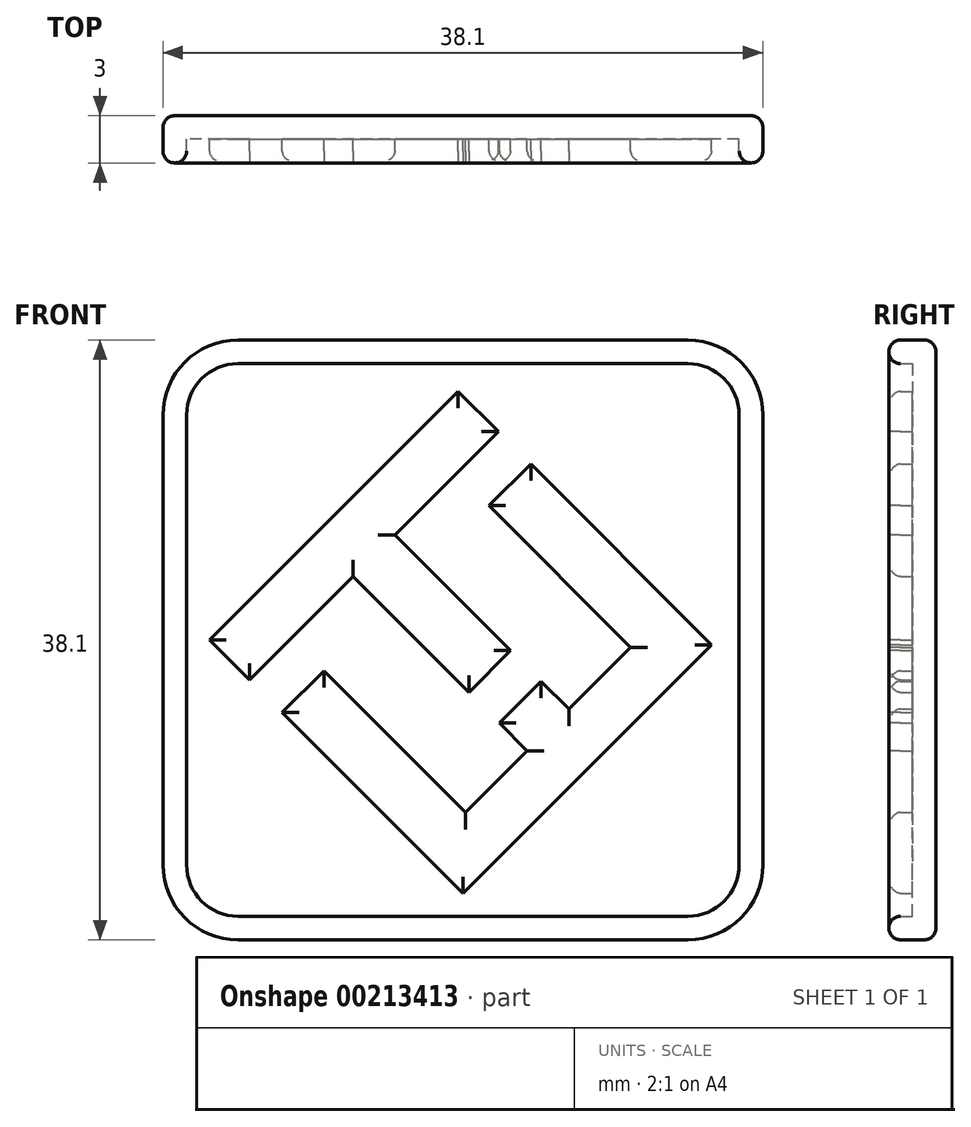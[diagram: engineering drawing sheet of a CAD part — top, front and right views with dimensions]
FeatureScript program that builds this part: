
annotation { "Feature Type Name" : "Feature", "Feature Type Description" : "" }
export const myFeature = defineFeature(function(context is Context, id is Id, definition is map)
    precondition{}
    {
        {
            var Q0;
            Q0=qCreatedBy(makeId("Front.planeOp"),FACE);
            var sketch = newSketch(context, id + "F0", { "sketchPlane" : qUnion([Q0])});
            skLineSegment(sketch, "E0", {"start": v(-14.29, -19.05) * mm, "end": v(14.29, -19.05) * mm});
            skArc(sketch, "E1", {"start": v(14.29, -19.05) * mm, "mid": v(17.66, -17.66) * mm, "end": v(19.05, -14.29) * mm});
            skLineSegment(sketch, "E2", {"start": v(19.05, -14.29) * mm, "end": v(19.05, 14.29) * mm});
            skArc(sketch, "E3", {"start": v(19.05, 14.29) * mm, "mid": v(17.66, 17.66) * mm, "end": v(14.29, 19.05) * mm});
            skLineSegment(sketch, "E4", {"start": v(14.29, 19.05) * mm, "end": v(-14.29, 19.05) * mm});
            skArc(sketch, "E5", {"start": v(-14.29, 19.05) * mm, "mid": v(-17.66, 17.66) * mm, "end": v(-19.05, 14.29) * mm});
            skLineSegment(sketch, "E6", {"start": v(-19.05, 14.29) * mm, "end": v(-19.05, -14.29) * mm});
            skArc(sketch, "E7", {"start": v(-19.05, -14.29) * mm, "mid": v(-17.66, -17.66) * mm, "end": v(-14.29, -19.05) * mm});
            skLineSegment(sketch, "E8", {"start": v(-13.55, -2.55) * mm, "end": v(-6.98, 4.02) * mm});
            skLineSegment(sketch, "E9", {"start": v(-6.98, 4.02) * mm, "end": v(0.37, -3.33) * mm});
            skLineSegment(sketch, "E10", {"start": v(0.37, -3.33) * mm, "end": v(3.03, -0.68) * mm});
            skLineSegment(sketch, "E11", {"start": v(3.03, -0.68) * mm, "end": v(-4.32, 6.67) * mm});
            skLineSegment(sketch, "E12", {"start": v(-13.55, -2.55) * mm, "end": v(-16.1, 0) * mm});
            skLineSegment(sketch, "E13", {"start": v(-16.1, 0) * mm, "end": v(-0.3, 15.8) * mm});
            skLineSegment(sketch, "E14", {"start": v(2.25, 13.24) * mm, "end": v(-0.3, 15.8) * mm});
            skLineSegment(sketch, "E15", {"start": v(-4.32, 6.67) * mm, "end": v(2.25, 13.24) * mm});
            skLineSegment(sketch, "E16", {"start": v(0, -16.1) * mm, "end": v(15.8, -0.3) * mm});
            skLineSegment(sketch, "E17", {"start": v(15.8, -0.3) * mm, "end": v(4.31, 11.17) * mm});
            skLineSegment(sketch, "E18", {"start": v(1.66, 8.52) * mm, "end": v(4.31, 11.17) * mm});
            skLineSegment(sketch, "E19", {"start": v(1.66, 8.52) * mm, "end": v(10.65, -0.47) * mm});
            skLineSegment(sketch, "E20", {"start": v(10.65, -0.47) * mm, "end": v(6.74, -4.39) * mm});
            skLineSegment(sketch, "E21", {"start": v(6.74, -4.39) * mm, "end": v(4.97, -2.62) * mm});
            skLineSegment(sketch, "E22", {"start": v(2.32, -5.27) * mm, "end": v(4.97, -2.62) * mm});
            skLineSegment(sketch, "E23", {"start": v(0, -16.1) * mm, "end": v(-11.48, -4.62) * mm});
            skLineSegment(sketch, "E24", {"start": v(-8.83, -1.97) * mm, "end": v(-11.48, -4.62) * mm});
            skLineSegment(sketch, "E25", {"start": v(-8.83, -1.97) * mm, "end": v(0.17, -10.96) * mm});
            skLineSegment(sketch, "E26", {"start": v(0.17, -10.96) * mm, "end": v(4.08, -7.04) * mm});
            skLineSegment(sketch, "E27", {"start": v(4.08, -7.04) * mm, "end": v(2.32, -5.27) * mm});
            skSolve(sketch);
        }
        {
            var Q0;
            Q0 = qSketchRegion(id + "F0", true);
            extrude(context, id + "F1", {"entities" : qUnion([Q0]), "depth" : 1.5 * mm});
        }
        {
            var Q0;
            Q0=makeQuery(id+"F0.imprint","IMPRINT",FACE,{"disambiguationData":[TD([[makeQuery(id+"F0.imprint","IMPRINT",EDGE,{"derivedFrom":sQuery(id+"F0.wireOp",EDGE,"E8")}),1.0]])]});
            var Q1;
            Q1=makeQuery(id+"F0.imprint","IMPRINT",FACE,{"disambiguationData":[TD([[makeQuery(id+"F0.imprint","IMPRINT",EDGE,{"derivedFrom":sQuery(id+"F0.wireOp",EDGE,"E16")}),1.0]])]});
            extrude(context, id + "F2", {"entities" : qUnion([Q0, Q1]), "operationType" : NewBodyOperationType.ADD, "depth" : 3 * mm});
        }
        {
            var Q0;
            Q0=makeQuery(id+"F0.imprint","IMPRINT",FACE,{"disambiguationData":[TD([[makeQuery(id+"F0.imprint","IMPRINT",EDGE,{"derivedFrom":sQuery(id+"F0.wireOp",EDGE,"E0")}),1.0]])]});
            var sketch = newSketch(context, id + "F3", { "sketchPlane" : qUnion([Q0])});
            skLineSegment(sketch, "E28.0.0", {"start": v(-19.05, 14.29) * mm, "end": v(-19.05, -14.29) * mm});
            skArc(sketch, "E28.0.1", {"start": v(-19.05, -14.29) * mm, "mid": v(-17.66, -17.66) * mm, "end": v(-14.29, -19.05) * mm});
            skLineSegment(sketch, "E28.0.2", {"start": v(-14.29, -19.05) * mm, "end": v(14.29, -19.05) * mm});
            skArc(sketch, "E28.0.3", {"start": v(14.29, -19.05) * mm, "mid": v(17.66, -17.66) * mm, "end": v(19.05, -14.29) * mm});
            skLineSegment(sketch, "E28.0.4", {"start": v(19.05, -14.29) * mm, "end": v(19.05, 14.29) * mm});
            skArc(sketch, "E28.0.5", {"start": v(19.05, 14.29) * mm, "mid": v(17.66, 17.66) * mm, "end": v(14.29, 19.05) * mm});
            skLineSegment(sketch, "E28.0.6", {"start": v(14.29, 19.05) * mm, "end": v(-14.29, 19.05) * mm});
            skArc(sketch, "E28.0.7", {"start": v(-14.29, 19.05) * mm, "mid": v(-17.66, 17.66) * mm, "end": v(-19.05, 14.29) * mm});
            skArc(sketch, "E29.0", {"start": v(-14.29, 17.55) * mm, "mid": v(-16.6, 16.6) * mm, "end": v(-17.55, 14.29) * mm});
            skLineSegment(sketch, "E29.1", {"start": v(14.29, 17.55) * mm, "end": v(-14.29, 17.55) * mm});
            skLineSegment(sketch, "E29.2", {"start": v(-17.55, 14.29) * mm, "end": v(-17.55, -14.29) * mm});
            skArc(sketch, "E29.3", {"start": v(17.55, 14.29) * mm, "mid": v(16.6, 16.6) * mm, "end": v(14.29, 17.55) * mm});
            skArc(sketch, "E29.4", {"start": v(-17.55, -14.29) * mm, "mid": v(-16.6, -16.6) * mm, "end": v(-14.29, -17.55) * mm});
            skLineSegment(sketch, "E29.5", {"start": v(-14.29, -17.55) * mm, "end": v(14.29, -17.55) * mm});
            skArc(sketch, "E29.6", {"start": v(14.29, -17.55) * mm, "mid": v(16.6, -16.6) * mm, "end": v(17.55, -14.29) * mm});
            skLineSegment(sketch, "E29.7", {"start": v(17.55, -14.29) * mm, "end": v(17.55, 14.29) * mm});
            skSolve(sketch);
        }
        {
            var Q0;
            Q0=makeQuery(id+"F3.imprint","IMPRINT",FACE,{"disambiguationData":[TD([[makeQuery(id+"F3.imprint","IMPRINT",EDGE,{"derivedFrom":sQuery(id+"F3.wireOp",EDGE,"E28.0.0")}),1.0]])]});
            extrude(context, id + "F4", {"entities" : qUnion([Q0]), "operationType" : NewBodyOperationType.ADD, "depth" : 3 * mm});
        }
        {
            var Q0;
            Q0=makeQuery(id+"F2.opExtrude","CAP_FACE",FACE,{"disambiguationData":[OSD([sQuery(id+"F0.wireOp",EDGE,"E16"),sQuery(id+"F0.wireOp",EDGE,"E17"),sQuery(id+"F0.wireOp",EDGE,"E18"),sQuery(id+"F0.wireOp",EDGE,"E19"),sQuery(id+"F0.wireOp",EDGE,"E20"),sQuery(id+"F0.wireOp",EDGE,"E21"),sQuery(id+"F0.wireOp",EDGE,"E22"),sQuery(id+"F0.wireOp",EDGE,"E23"),sQuery(id+"F0.wireOp",EDGE,"E24"),sQuery(id+"F0.wireOp",EDGE,"E25"),sQuery(id+"F0.wireOp",EDGE,"E26"),sQuery(id+"F0.wireOp",EDGE,"E27")])],"isStart":false});
            var Q1;
            Q1=makeQuery(id+"F2.opExtrude","CAP_FACE",FACE,{"disambiguationData":[OSD([sQuery(id+"F0.wireOp",EDGE,"E8"),sQuery(id+"F0.wireOp",EDGE,"E9"),sQuery(id+"F0.wireOp",EDGE,"E10"),sQuery(id+"F0.wireOp",EDGE,"E11"),sQuery(id+"F0.wireOp",EDGE,"E12"),sQuery(id+"F0.wireOp",EDGE,"E13"),sQuery(id+"F0.wireOp",EDGE,"E14"),sQuery(id+"F0.wireOp",EDGE,"E15")])],"isStart":false});
            var Q2;
            Q2=makeQuery(id+"F4.opExtrude","CAP_FACE",FACE,{"disambiguationData":[OSD([sQuery(id+"F3.wireOp",EDGE,"E28.0.0"),sQuery(id+"F3.wireOp",EDGE,"E28.0.1"),sQuery(id+"F3.wireOp",EDGE,"E28.0.2"),sQuery(id+"F3.wireOp",EDGE,"E28.0.3"),sQuery(id+"F3.wireOp",EDGE,"E28.0.4"),sQuery(id+"F3.wireOp",EDGE,"E28.0.5"),sQuery(id+"F3.wireOp",EDGE,"E28.0.6"),sQuery(id+"F3.wireOp",EDGE,"E28.0.7"),sQuery(id+"F3.wireOp",EDGE,"E29.0"),sQuery(id+"F3.wireOp",EDGE,"E29.1"),sQuery(id+"F3.wireOp",EDGE,"E29.2"),sQuery(id+"F3.wireOp",EDGE,"E29.3"),sQuery(id+"F3.wireOp",EDGE,"E29.4"),sQuery(id+"F3.wireOp",EDGE,"E29.5"),sQuery(id+"F3.wireOp",EDGE,"E29.6"),sQuery(id+"F3.wireOp",EDGE,"E29.7")])],"isStart":false});
            fillet(context, id + "F5", {"entities" : qUnion([Q0, Q1, Q2]), "radius" : .75 * mm, "tangentPropagation" : true, "allowEdgeOverflow" : false});
        }
        {
            var Q0;
            {var subQ0=sQuery(id+"F0.wireOp",EDGE,"E27");var subQ1=sQuery(id+"F0.wireOp",EDGE,"E26");var subQ2=sQuery(id+"F0.wireOp",EDGE,"E25");var subQ3=sQuery(id+"F0.wireOp",EDGE,"E24");var subQ4=sQuery(id+"F0.wireOp",EDGE,"E23");var subQ5=sQuery(id+"F0.wireOp",EDGE,"E22");var subQ6=sQuery(id+"F0.wireOp",EDGE,"E21");var subQ7=sQuery(id+"F0.wireOp",EDGE,"E20");var subQ8=sQuery(id+"F0.wireOp",EDGE,"E19");var subQ9=sQuery(id+"F0.wireOp",EDGE,"E18");var subQ10=sQuery(id+"F0.wireOp",EDGE,"E17");var subQ11=sQuery(id+"F0.wireOp",EDGE,"E16");var subQ12=sQuery(id+"F0.wireOp",EDGE,"E15");var subQ13=sQuery(id+"F0.wireOp",EDGE,"E14");var subQ14=sQuery(id+"F0.wireOp",EDGE,"E13");var subQ15=sQuery(id+"F0.wireOp",EDGE,"E12");var subQ16=sQuery(id+"F0.wireOp",EDGE,"E11");var subQ17=sQuery(id+"F0.wireOp",EDGE,"E10");var subQ18=sQuery(id+"F0.wireOp",EDGE,"E9");var subQ19=sQuery(id+"F0.wireOp",EDGE,"E8");Q0=makeQuery(id+"F2.boolean.opBoolean","MERGE",FACE,{"derivedFrom":[makeQuery(id+"F1.opExtrude","CAP_FACE",FACE,{"disambiguationData":[OSD([sQuery(id+"F0.wireOp",EDGE,"E0"),sQuery(id+"F0.wireOp",EDGE,"E1"),sQuery(id+"F0.wireOp",EDGE,"E2"),sQuery(id+"F0.wireOp",EDGE,"E3"),sQuery(id+"F0.wireOp",EDGE,"E4"),sQuery(id+"F0.wireOp",EDGE,"E5"),sQuery(id+"F0.wireOp",EDGE,"E6"),sQuery(id+"F0.wireOp",EDGE,"E7"),subQ19,subQ18,subQ17,subQ16,subQ15,subQ14,subQ13,subQ12,subQ11,subQ10,subQ9,subQ8,subQ7,subQ6,subQ5,subQ4,subQ3,subQ2,subQ1,subQ0])],"isStart":true}),makeQuery(id+"F2.opExtrude","CAP_FACE",FACE,{"disambiguationData":[OSD([subQ19,subQ18,subQ17,subQ16,subQ15,subQ14,subQ13,subQ12])],"isStart":true}),makeQuery(id+"F2.opExtrude","CAP_FACE",FACE,{"disambiguationData":[OSD([subQ11,subQ10,subQ9,subQ8,subQ7,subQ6,subQ5,subQ4,subQ3,subQ2,subQ1,subQ0])],"isStart":true})]});}
            fillet(context, id + "F6", {"entities" : qUnion([Q0]), "radius" : .75 * mm, "tangentPropagation" : true, "allowEdgeOverflow" : false});
        }
    });
